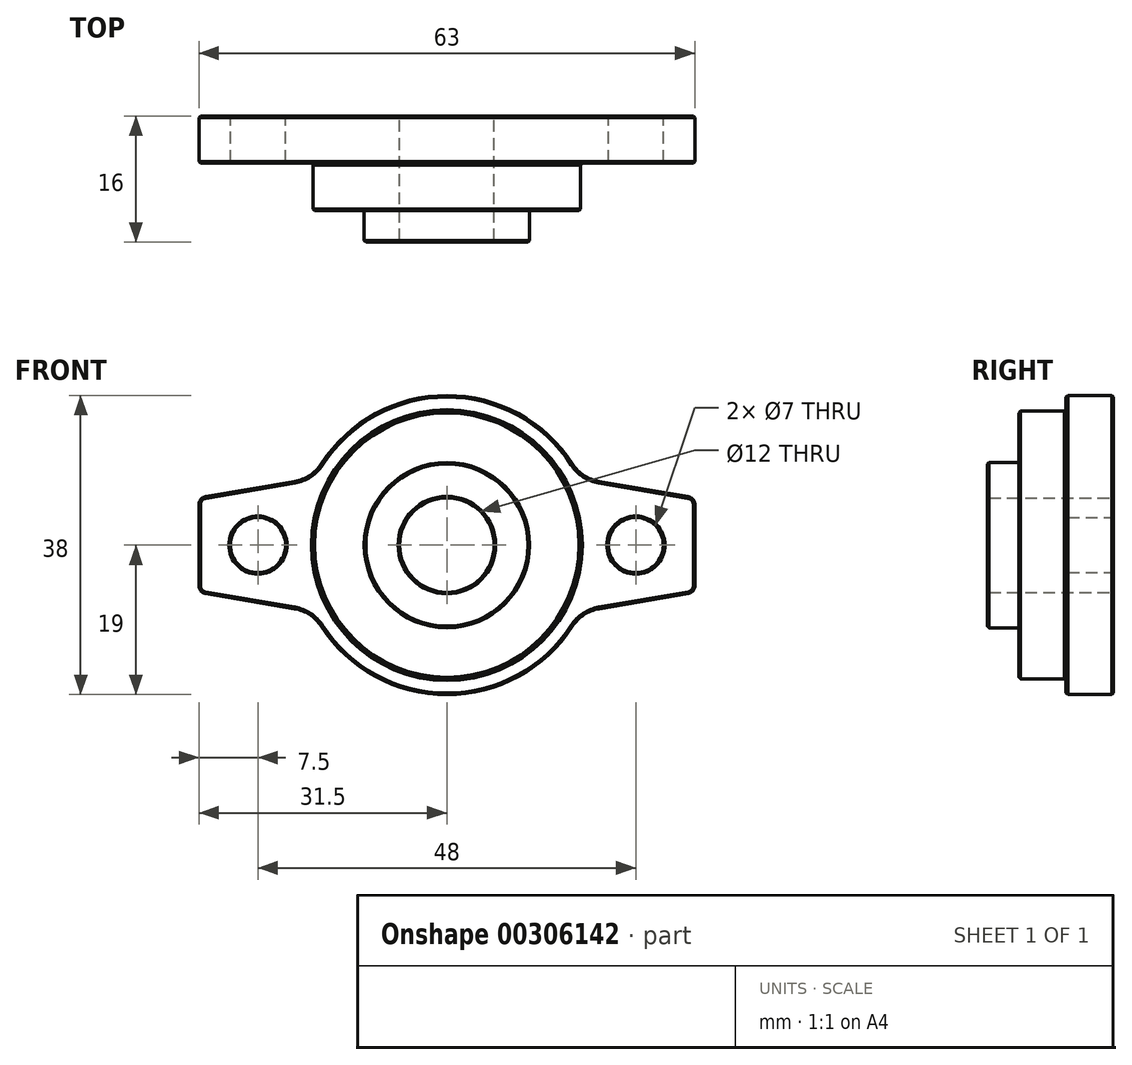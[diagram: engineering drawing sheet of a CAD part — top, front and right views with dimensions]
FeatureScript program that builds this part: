
annotation { "Feature Type Name" : "Feature", "Feature Type Description" : "" }
export const myFeature = defineFeature(function(context is Context, id is Id, definition is map)
    precondition{}
    {
        {
            var Q0;
            Q0=qCreatedBy(makeId("Front.planeOp"),FACE);
            var sketch = newSketch(context, id + "F0", { "sketchPlane" : qUnion([Q0])});
            skPoint(sketch, "E0", {"position": v(-24, 0) * mm});
            skPoint(sketch, "E1", {"position": v(24, 0) * mm});
            skCircle(sketch, "E2", {"center": v(-24, 0) * mm, "radius": 3.5 * mm});
            skCircle(sketch, "E3", {"center": v(24, 0) * mm, "radius": 3.5 * mm});
            skPoint(sketch, "E4", {"position": v(-31.5, 0) * mm});
            skPoint(sketch, "E5", {"position": v(31.5, 0) * mm});
            skLineSegment(sketch, "E6", {"start": v(-31.5, -6) * mm, "end": v(-31.5, 6) * mm});
            skLineSegment(sketch, "E7", {"start": v(31.5, 6) * mm, "end": v(31.5, -6) * mm});
            skCircle(sketch, "E8", {"center": v(0, 0) * mm, "radius": 19 * mm});
            skCircle(sketch, "E9", {"center": v(0, 0) * mm, "radius": 8 * mm});
            skPoint(sketch, "E10", {"position": v(-17, 8.49) * mm});
            skPoint(sketch, "E11", {"position": v(-17, -8.49) * mm});
            skPoint(sketch, "E12", {"position": v(17, -8.49) * mm});
            skPoint(sketch, "E13", {"position": v(17, 8.49) * mm});
            skLineSegment(sketch, "E14", {"start": v(-31.5, 6) * mm, "end": v(-17, 8.49) * mm});
            skLineSegment(sketch, "E15", {"start": v(-31.5, -6) * mm, "end": v(-17, -8.49) * mm});
            skLineSegment(sketch, "E16", {"start": v(17, -8.49) * mm, "end": v(31.5, -6) * mm});
            skLineSegment(sketch, "E17", {"start": v(17, 8.49) * mm, "end": v(31.5, 6) * mm});
            skCircle(sketch, "E18", {"center": v(0, 0) * mm, "radius": 10.5 * mm});
            skSolve(sketch);
        }
        {
            var Q0;
            Q0=makeQuery(id+"F0.imprint","IMPRINT",FACE,{"disambiguationData":[TD([[makeQuery(id+"F0.imprint","IMPRINT",EDGE,{"derivedFrom":sQuery(id+"F0.wireOp",EDGE,"E2")}),-1.0]])]});
            var Q1;
            Q1=makeQuery(id+"F0.imprint","IMPRINT",FACE,{"disambiguationData":[TD([[makeQuery(id+"F0.imprint","IMPRINT",EDGE,{"derivedFrom":sQuery(id+"F0.wireOp",EDGE,"E18")}),-1.0]])]});
            var Q2;
            Q2=makeQuery(id+"F0.imprint","IMPRINT",FACE,{"disambiguationData":[TD([[makeQuery(id+"F0.imprint","IMPRINT",EDGE,{"derivedFrom":sQuery(id+"F0.wireOp",EDGE,"E3")}),-1.0]])]});
            extrude(context, id + "F1", {"entities" : qUnion([Q0, Q1, Q2]), "depth" : 6 * mm});
        }
        {
            var Q0;
            Q0=qCreatedBy(makeId("Front.planeOp"),FACE);
            var sketch = newSketch(context, id + "F2", { "sketchPlane" : qUnion([Q0])});
            skCircle(sketch, "E19", {"center": v(0, 0) * mm, "radius": 10.5 * mm});
            skCircle(sketch, "E20", {"center": v(0, 0) * mm, "radius": 6 * mm});
            skSolve(sketch);
        }
        {
            var Q0;
            Q0=makeQuery(id+"F2.imprint","IMPRINT",FACE,{"disambiguationData":[TD([[makeQuery(id+"F2.imprint","IMPRINT",EDGE,{"derivedFrom":sQuery(id+"F2.wireOp",EDGE,"E19")}),1.0]])]});
            extrude(context, id + "F3", {"entities" : qUnion([Q0]), "operationType" : NewBodyOperationType.ADD, "depth" : 16 * mm});
        }
        {
            var Q0;
            Q0=makeQuery(id+"F1.opExtrude","CAP_FACE",FACE,{"disambiguationData":[OSD([sQuery(id+"F0.wireOp",EDGE,"E2"),sQuery(id+"F0.wireOp",EDGE,"E3"),sQuery(id+"F0.wireOp",EDGE,"E6"),sQuery(id+"F0.wireOp",EDGE,"E7"),sQuery(id+"F0.wireOp",EDGE,"E8"),sQuery(id+"F0.wireOp",EDGE,"E14"),sQuery(id+"F0.wireOp",EDGE,"E15"),sQuery(id+"F0.wireOp",EDGE,"E16"),sQuery(id+"F0.wireOp",EDGE,"E17"),sQuery(id+"F0.wireOp",EDGE,"E18")])],"isStart":false});
            var sketch = newSketch(context, id + "F4", { "sketchPlane" : qUnion([Q0])});
            skCircle(sketch, "E21", {"center": v(0, 0) * mm, "radius": 17 * mm});
            skCircle(sketch, "E22", {"center": v(0, 0) * mm, "radius": 10.5 * mm});
            skSolve(sketch);
        }
        {
            var Q0;
            Q0=makeQuery(id+"F4.imprint","IMPRINT",FACE,{"disambiguationData":[TD([[makeQuery(id+"F4.imprint","IMPRINT",EDGE,{"derivedFrom":sQuery(id+"F4.wireOp",EDGE,"E21")}),1.0]])]});
            extrude(context, id + "F5", {"entities" : qUnion([Q0]), "operationType" : NewBodyOperationType.ADD, "depth" : 6 * mm});
        }
        {
            var Q0;
            Q0=makeQuery(id+"F1.opExtrude","SWEPT_EDGE",EDGE,{"disambiguationData":[OSD([sQuery(id+"F0.wireOp",EDGE,"E8"),sQuery(id+"F0.wireOp",EDGE,"E15")])]});
            var Q1;
            Q1=makeQuery(id+"F1.opExtrude","SWEPT_EDGE",EDGE,{"disambiguationData":[OSD([sQuery(id+"F0.wireOp",EDGE,"E8"),sQuery(id+"F0.wireOp",EDGE,"E16")])]});
            var Q2;
            Q2=makeQuery(id+"F1.opExtrude","SWEPT_EDGE",EDGE,{"disambiguationData":[OSD([sQuery(id+"F0.wireOp",EDGE,"E8"),sQuery(id+"F0.wireOp",EDGE,"E17")])]});
            var Q3;
            Q3=makeQuery(id+"F1.opExtrude","SWEPT_EDGE",EDGE,{"disambiguationData":[OSD([sQuery(id+"F0.wireOp",EDGE,"E8"),sQuery(id+"F0.wireOp",EDGE,"E14")])]});
            fillet(context, id + "F6", {"entities" : qUnion([Q0, Q1, Q2, Q3]), "radius" : 5 * mm, "tangentPropagation" : true, "allowEdgeOverflow" : false});
        }
        {
            var Q0;
            Q0=makeQuery(id+"F1.opExtrude","SWEPT_EDGE",EDGE,{"disambiguationData":[OSD([sQuery(id+"F0.wireOp",EDGE,"E6"),sQuery(id+"F0.wireOp",EDGE,"E15")])]});
            var Q1;
            Q1=makeQuery(id+"F1.opExtrude","SWEPT_EDGE",EDGE,{"disambiguationData":[OSD([sQuery(id+"F0.wireOp",EDGE,"E7"),sQuery(id+"F0.wireOp",EDGE,"E16")])]});
            var Q2;
            Q2=makeQuery(id+"F1.opExtrude","SWEPT_EDGE",EDGE,{"disambiguationData":[OSD([sQuery(id+"F0.wireOp",EDGE,"E7"),sQuery(id+"F0.wireOp",EDGE,"E17")])]});
            var Q3;
            Q3=makeQuery(id+"F1.opExtrude","SWEPT_EDGE",EDGE,{"disambiguationData":[OSD([sQuery(id+"F0.wireOp",EDGE,"E6"),sQuery(id+"F0.wireOp",EDGE,"E14")])]});
            fillet(context, id + "F7", {"entities" : qUnion([Q0, Q1, Q2, Q3]), "radius" : 1 * mm, "tangentPropagation" : true, "allowEdgeOverflow" : false});
        }
        {
            var Q0;
            Q0=makeQuery(id+"F5.opExtrude","CAP_EDGE",EDGE,{"disambiguationData":[OSD([sQuery(id+"F4.wireOp",EDGE,"E21")])],"isStart":false});
            var Q1;
            Q1=makeQuery(id+"F1.opExtrude","CAP_FACE",FACE,{"disambiguationData":[OSD([sQuery(id+"F0.wireOp",EDGE,"E2"),sQuery(id+"F0.wireOp",EDGE,"E3"),sQuery(id+"F0.wireOp",EDGE,"E6"),sQuery(id+"F0.wireOp",EDGE,"E7"),sQuery(id+"F0.wireOp",EDGE,"E8"),sQuery(id+"F0.wireOp",EDGE,"E14"),sQuery(id+"F0.wireOp",EDGE,"E15"),sQuery(id+"F0.wireOp",EDGE,"E16"),sQuery(id+"F0.wireOp",EDGE,"E17"),sQuery(id+"F0.wireOp",EDGE,"E18")])],"isStart":false});
            var Q2;
            Q2=makeQuery(id+"F3.boolean.opBoolean","MERGE",FACE,{"derivedFrom":[makeQuery(id+"F1.opExtrude","CAP_FACE",FACE,{"disambiguationData":[OSD([sQuery(id+"F0.wireOp",EDGE,"E2"),sQuery(id+"F0.wireOp",EDGE,"E3"),sQuery(id+"F0.wireOp",EDGE,"E6"),sQuery(id+"F0.wireOp",EDGE,"E7"),sQuery(id+"F0.wireOp",EDGE,"E8"),sQuery(id+"F0.wireOp",EDGE,"E14"),sQuery(id+"F0.wireOp",EDGE,"E15"),sQuery(id+"F0.wireOp",EDGE,"E16"),sQuery(id+"F0.wireOp",EDGE,"E17"),sQuery(id+"F0.wireOp",EDGE,"E18")])],"isStart":true}),makeQuery(id+"F3.opExtrude","CAP_FACE",FACE,{"disambiguationData":[OSD([sQuery(id+"F2.wireOp",EDGE,"E19"),sQuery(id+"F2.wireOp",EDGE,"E20")])],"isStart":true})]});
            chamfer(context, id + "F8", {"entities" : qUnion([Q0, Q1, Q2]), "width" : 0.2 * mm, "tangentPropagation" : true});
        }
        {
            var Q0;
            Q0=makeQuery(id+"F3.opExtrude","CAP_FACE",FACE,{"disambiguationData":[OSD([sQuery(id+"F2.wireOp",EDGE,"E19"),sQuery(id+"F2.wireOp",EDGE,"E20")])],"isStart":false});
            chamfer(context, id + "F9", {"entities" : qUnion([Q0]), "width" : 0.2 * mm, "tangentPropagation" : true});
        }
    });
